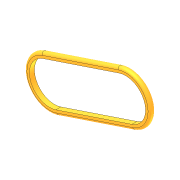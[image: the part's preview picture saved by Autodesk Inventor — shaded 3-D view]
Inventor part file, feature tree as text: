
AUTODESK INVENTOR PART (.ipt)
format: ipt  version: 2012 (Build 160160000, 160)  size: 104,448 bytes
history: native  units: in
note: dims shown in document units (in); Inventor stores cm internally (conversion verified against a paired STEP export)
features: extrude x1, fillet x1, sketch x1
ambient origin geometry x8: Origin, YZ Plane, XZ Plane, XY Plane, X Axis, Y Axis, Z Axis, Center Point
bodies: Solid1 (feature_tree)
feature tree (3):
  extrude  "Extrusion1"  Depth=3.0in
  fillet  "Fillet1"  Radius=0.1875in
  sketch  "Sketch1"  dims[d0=0.75in d1=3.0in d2=0.1875in d3=0.1875in d4=0.0in d5=0.0938in]
